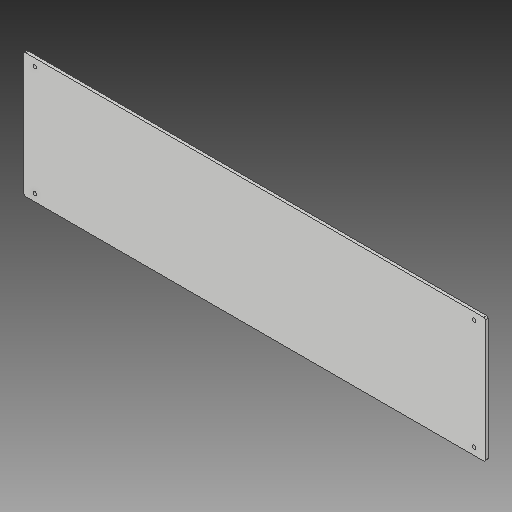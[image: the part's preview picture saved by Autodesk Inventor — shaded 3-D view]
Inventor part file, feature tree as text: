
AUTODESK INVENTOR PART (.ipt)
format: ipt  version: 2019 (Build 230136000, 136)  size: 116,736 bytes
history: native  units: in
note: dims shown in document units (in); Inventor stores cm internally (conversion verified against a paired STEP export)
features: reference x3, other x3, extrude x1, fillet x1, sketch x1, helix x1
ambient origin geometry x8: Origin, YZ Plane, XZ Plane, XY Plane, X Axis, Y Axis, Z Axis, Center Point
bodies: Solid1 (feature_tree)
feature tree (10):
  extrude  "Extrusion1"  Depth=0.0787in
  fillet  "Fillet1"  Radius=0.1969in
  sketch  "Sketch1"  dims[d0=6.6929in d1=0.1969in d2=0.1969in d3=0.1969in d4=0.1969in d5=0.3937in d6=0.3937in d7=0.3937in d8=0.3937in d9=0.1575in d10=0.0in d11=0.0787in]
  reference  "Reference1"
  reference  "Reference2"
  reference  "Reference3"
  other  "<userpath>\Documents\CAD Files\Helix DLP\Helix DLP.iam"
  helix  "Helix DLP.iam"  [1 undecoded]
  other  "30X30 - T-slot - Aluminium Profile_CPY_CPY_CPY_CPY:2"
  other  "30X30 - T-slot - Aluminium Profile_CPY_CPY_CPY_CPY:1"
note: 1 required parameter value undecoded (feature->parameter linkage not recoverable at this tier; creation-order binding heuristic only, values carry confidence <= 0.55)
